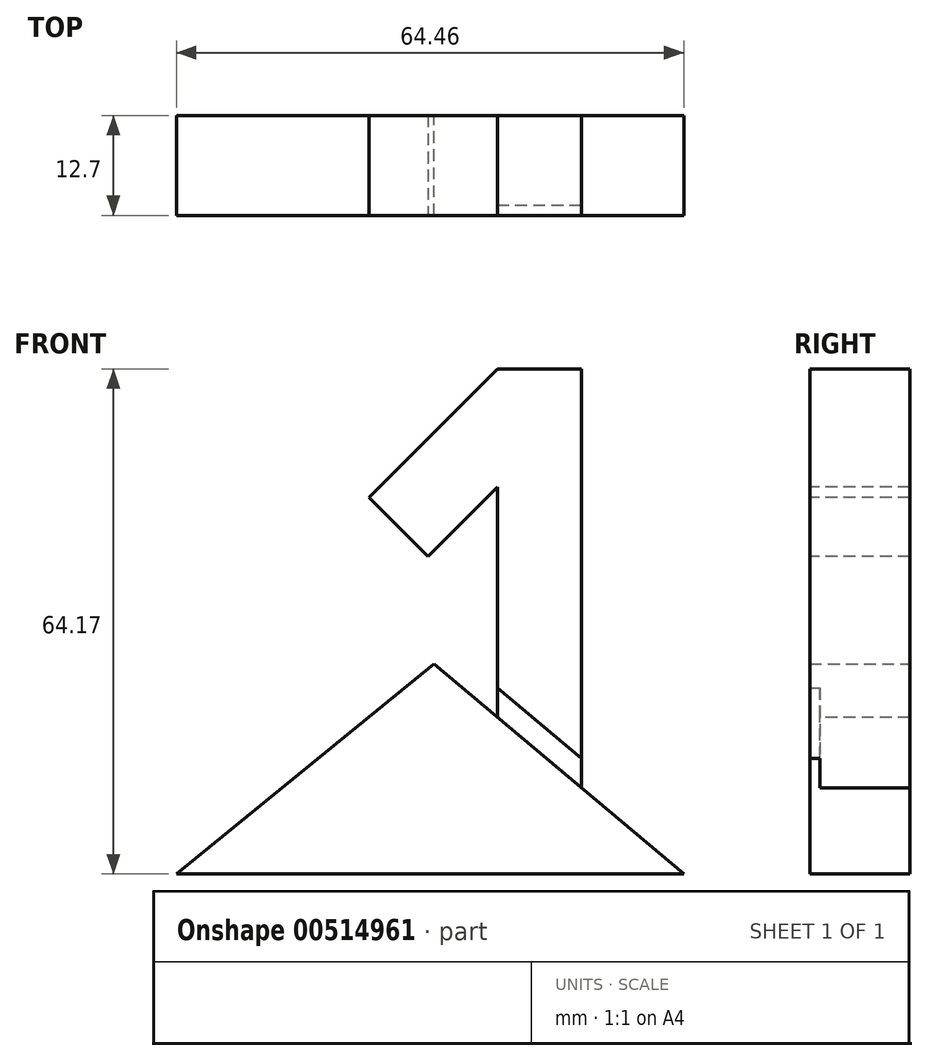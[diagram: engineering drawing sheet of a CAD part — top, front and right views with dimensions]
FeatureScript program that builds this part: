
annotation { "Feature Type Name" : "Feature", "Feature Type Description" : "" }
export const myFeature = defineFeature(function(context is Context, id is Id, definition is map)
    precondition{}
    {
        {
            var Q0;
            Q0=qCreatedBy(makeId("Front.planeOp"),FACE);
            var sketch = newSketch(context, id + "F0", { "sketchPlane" : qUnion([Q0])});
            skText(sketch, "E0", { "text": "1", "fontName": "AllertaStencil-Regular.ttf"});
            skLineSegment(sketch, "E1", {"start": v(0, 0) * mm, "end": v(-32.7, -26.7) * mm});
            skLineSegment(sketch, "E2", {"start": v(-32.7, -26.7) * mm, "end": v(31.76, -26.7) * mm});
            skLineSegment(sketch, "E3", {"start": v(31.76, -26.7) * mm, "end": v(0, 0) * mm});
            skLineSegment(sketch, "E4", {"start": v(0, 3.75) * mm, "end": v(36.25, -26.72) * mm});
            const initialGuessF0  = {"E0": [-0.01078, -0.02687, 1, 0, 0.06438]};
            skSetInitialGuess(sketch, initialGuessF0);
            skSolve(sketch);
        }
        {
            var Q0;
            {var subQ5=sQuery(id+"F0.wireOp",EDGE,"E1");Q0=makeQuery(id+"F0.imprint","IMPRINT",FACE,{"disambiguationData":[TD([[makeQuery(id+"F0.imprint","IMPRINT",EDGE,{"derivedFrom":subQ5}),1.0]])]});}
            var Q1;
            {var subQ0=sQuery(id+"F0.wireOp",EDGE,"E2");var subQ1=sQuery(id+"F0.wireOp",EDGE,"E0.sketch_text.stroke-1");var subQ2=makeQuery(id+"F0.imprint","INTERSECT",VERTEX,{"derivedFrom":[subQ1,subQ0]});Q1=makeQuery(id+"F0.imprint","IMPRINT",FACE,{"disambiguationData":[TD([[makeQuery(id+"F0.imprint","IMPRINT",EDGE,{"disambiguationData":[TD([[subQ2,-1.0]])],"derivedFrom":subQ1}),-1.0]])]});}
            var Q2;
            {var subQ0=sQuery(id+"F0.wireOp",EDGE,"E3");var subQ1=sQuery(id+"F0.wireOp",EDGE,"E0.sketch_text.stroke-6");var subQ2=makeQuery(id+"F0.imprint","INTERSECT",VERTEX,{"derivedFrom":[subQ1,subQ0]});Q2=makeQuery(id+"F0.imprint","IMPRINT",FACE,{"disambiguationData":[TD([[makeQuery(id+"F0.imprint","IMPRINT",EDGE,{"disambiguationData":[TD([[subQ2,-1.0]])],"derivedFrom":subQ1}),1.0]])]});}
            extrude(context, id + "F1", {"entities" : qUnion([Q0, Q1, Q2]), "endBound" : BoundingType.SYMMETRIC, "depth" : 12.7 * mm, "offsetDistance" : 25.4 * mm});
        }
        {
            var Q0;
            {var subQ0=sQuery(id+"F0.wireOp",EDGE,"E0.sketch_text.stroke-2");Q0=makeQuery(id+"F0.imprint","IMPRINT",FACE,{"disambiguationData":[TD([[makeQuery(id+"F0.imprint","IMPRINT",EDGE,{"derivedFrom":subQ0}),-1.0]])]});}
            var Q1;
            {var subQ0=sQuery(id+"F0.wireOp",EDGE,"E4");var subQ1=sQuery(id+"F0.wireOp",EDGE,"E0.sketch_text.stroke-1");var subQ2=makeQuery(id+"F0.imprint","INTERSECT",VERTEX,{"derivedFrom":[subQ1,subQ0]});Q1=makeQuery(id+"F0.imprint","IMPRINT",FACE,{"disambiguationData":[TD([[makeQuery(id+"F0.imprint","IMPRINT",EDGE,{"disambiguationData":[TD([[subQ2,1.0]])],"derivedFrom":subQ1}),-1.0]])]});}
            var Q2;
            Q2=makeQuery(id+"F1.opExtrude","CAP_FACE",FACE,{"disambiguationData":[OSD([sQuery(id+"F0.wireOp",EDGE,"E1"),sQuery(id+"F0.wireOp",EDGE,"E2"),sQuery(id+"F0.wireOp",EDGE,"E3")])],"isStart":true});
            extrude(context, id + "F2", {"entities" : qUnion([Q0, Q1]), "operationType" : NewBodyOperationType.ADD, "endBound" : BoundingType.UP_TO_SURFACE, "oppositeDirection" : true, "depth" : 9.27 * mm, "endBoundEntityFace" : qUnion([Q2]), "offsetDistance" : 25.4 * mm});
        }
        {
            var Q0;
            {var subQ0=sQuery(id+"F0.wireOp",EDGE,"E0.sketch_text.stroke-2");Q0=makeQuery(id+"F0.imprint","IMPRINT",FACE,{"disambiguationData":[TD([[makeQuery(id+"F0.imprint","IMPRINT",EDGE,{"derivedFrom":subQ0}),-1.0]])]});}
            extrude(context, id + "F3", {"entities" : qUnion([Q0]), "operationType" : NewBodyOperationType.ADD, "endBound" : BoundingType.SYMMETRIC, "depth" : 12.7 * mm, "offsetDistance" : 25.4 * mm});
        }
        {
            var Q0;
            {var subQ0=sQuery(id+"F0.wireOp",EDGE,"E4");var subQ1=sQuery(id+"F0.wireOp",EDGE,"E0.sketch_text.stroke-1");var subQ2=makeQuery(id+"F0.imprint","INTERSECT",VERTEX,{"derivedFrom":[subQ1,subQ0]});Q0=makeQuery(id+"F0.imprint","IMPRINT",FACE,{"disambiguationData":[TD([[makeQuery(id+"F0.imprint","IMPRINT",EDGE,{"disambiguationData":[TD([[subQ2,1.0]])],"derivedFrom":subQ1}),-1.0]])]});}
            extrude(context, id + "F4", {"entities" : qUnion([Q0]), "operationType" : NewBodyOperationType.ADD, "depth" : 5.08 * mm, "offsetDistance" : 25.4 * mm});
        }
    });
